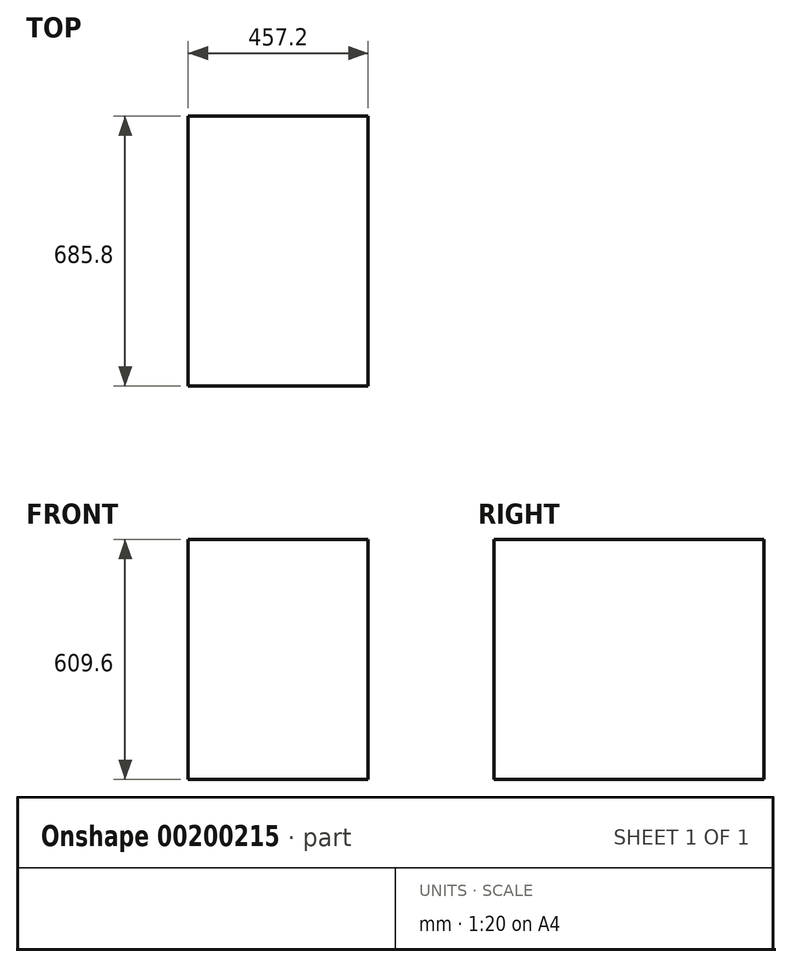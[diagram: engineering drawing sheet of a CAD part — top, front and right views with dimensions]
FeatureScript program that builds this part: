
annotation { "Feature Type Name" : "Feature", "Feature Type Description" : "" }
export const myFeature = defineFeature(function(context is Context, id is Id, definition is map)
    precondition{}
    {
        {
            var Q0;
            Q0=qCreatedBy(makeId("Front.planeOp"),FACE);
            var sketch = newSketch(context, id + "F0", { "sketchPlane" : qUnion([Q0])});
            skLineSegment(sketch, "E0.bottom", {"start": v(-232, 424.96) * mm, "end": v(225.2, 424.96) * mm});
            skLineSegment(sketch, "E0.top", {"start": v(-232, -184.64) * mm, "end": v(225.2, -184.64) * mm});
            skLineSegment(sketch, "E0.left", {"start": v(-232, 424.96) * mm, "end": v(-232, -184.64) * mm});
            skLineSegment(sketch, "E0.right", {"start": v(225.2, 424.96) * mm, "end": v(225.2, -184.64) * mm});
            skSolve(sketch);
        }
        {
            var Q0;
            Q0=makeQuery(id+"F0.imprint","IMPRINT",FACE,{"disambiguationData":[TD([[makeQuery(id+"F0.imprint","IMPRINT",EDGE,{"derivedFrom":sQuery(id+"F0.wireOp",EDGE,"E0.bottom")}),-1.0]])]});
            extrude(context, id + "F1", {"entities" : qUnion([Q0]), "depth" : 685.8 * mm});
        }
    });
